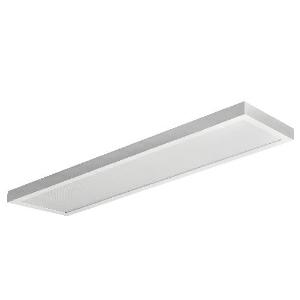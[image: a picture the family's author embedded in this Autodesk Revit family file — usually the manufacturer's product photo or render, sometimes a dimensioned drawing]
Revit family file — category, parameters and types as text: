
# Revit family: ledpanels-sf-p_l12-40w-dali-830_840_542003156000_e2d2
name_source: partatom
category: Lighting Fixtures
units: mm (PartAtom-declared; Revit-internal decimal feet)

## family parameters
Cut with Voids When Loaded = No
Host = Face
Light Source = No
Part Type = Normal
Room Calculation Point = No
Round Connector Dimension = Use Diameter
Shared = No

## types (1)
- LEDPanelS-Sf-P L12-40W-DALI-830/840 (1 x LED, 5000 lm, 4000)
    Apparent Load = 40 VA
    Approval mark = CE, ENEC
    CIE Flux Codes = 60 87 97 100 100
    Color Rendering = 80
    Color Temperature = 4000
    Control Gear = Electronic ballast
    Default Elevation = 1800 mm
    Description = Panel Performer Surface Mounted 1274x370mm-40W-5000lm-3/4000K-DALI
    Frequency = 60 Hz
    Height = 55 mm
    Lamp = 1 x LED
    Lamp Light Flux = 5000 lm
    Lamp count = 1
    Length = 1274 mm
    Luminous efficacy = 125 lm/W
    Manufacturer = OPPLE
    ModVariant = No
    Model = 542003156000
    Mounting Place = Ceiling
    Mounting Type = Surface mounted
    Number of Poles = 1
    OnlyDefault = Yes
    Power Factor = 1
    Product Name = LEDPanelS-Sf-P L12-40W-DALI-830/840
    Product group = Ceiling mounted luminaire
    ProductGroupID = 3
    Protection Class = Protection class II
    Protection Degree = IP 20
    RLX_Detail_Level = 1
    RLX_Emergency_Light_Flux = 0 lm
    RLX_Emergency_Type = 0
    RLX_Emergency_Type_DB = No
    RlxData = <blob elided: 96009 chars, md5=cd9f0438>
    Socket = socket
    Standby Power = 0 W
    System Light Flux = 5000 lm
    System Power = 40 W
    Type Comments = Product without accessories
    Type Image = web_surface_pl.jpg
    URL = http://relux.com
    VarID = ---
    Voltage = 230 V
    Voltage Range = 220-240 V
    Weight = 0.00 kg
    Width = 370 mm

## geometry (parser evidence)
native form markers: Blend x4, Sweep x9
no freeform markers — native parametric forms only
